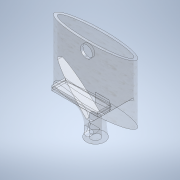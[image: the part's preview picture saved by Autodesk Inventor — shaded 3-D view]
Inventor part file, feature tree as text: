
AUTODESK INVENTOR PART (.ipt)
format: ipt  version: 2020 (Build 240168000, 168)  size: 277,504 bytes
history: native  units: mm
features: sketch x11, extrude x8, plane x3, chamfer x2, thicken_offset x2, loft x1, direct_edit x1, move_body x1
ambient origin geometry x8: Origin, YZ Plane, XZ Plane, XY Plane, X Axis, Y Axis, Z Axis, Center Point
bodies: Solid1 (feature_tree)
feature tree (29):
  sketch  "Sketch1"  dims[d0=20.0mm d1=20.0mm]
  plane  "Work Plane1"
  sketch  "Sketch2"  dims[d2=20.0mm d3=10.0mm]
  plane  "Work Plane2"
  loft  "Loft1"
  extrude  "Extrusion1"  Depth=10.0mm
  extrude  "Extrusion2"  Depth=10.0mm
  extrude  "Extrusion3"  TaperAngle=0.0deg  [1 undecoded]
  extrude  "Extrusion4"  Depth=10.0mm
  chamfer  "Chamfer1"  Distance=30.75mm
  chamfer  "Chamfer2"  Distance=30.0mm
  thicken_offset  "Thicken1"
  thicken_offset  "Thicken2"
  plane  "Work Plane3"
  extrude  "Extrusion5"  Depth=16.0mm TaperAngle=0.0deg
  extrude  "Extrusion6"  Depth=16.0mm TaperAngle=45.0deg
  extrude  "Extrusion7"  Depth=20.0mm
  direct_edit  "Direct Edit1"
  extrude  "Extrusion8"  Depth=20.0mm
  sketch  "Sketch3"  dims[d4=45.0mm d5=10.0mm]
  sketch  "Sketch4"  dims[d6=0.0mm d7=90.0deg d8=0.0mm d9=90.0deg]
  sketch  "Sketch5"  dims[d10=0.0mm d11=90.0deg d12=10.0mm d13=30.75mm d14=0.0mm d15=30.0mm d16=0.0mm]
  sketch  "Sketch6"  dims[d17=25.0mm d18=0.0mm d19=16.0mm d20=0.0mm]
  sketch  "Sketch7"  dims[d21=16.0mm d22=2.0mm d23=45.0deg d24=16.0mm d25=2.0mm d26=45.0deg]
  sketch  "Sketch8"  dims[d27=20.0mm d28=20.0mm]
  sketch  "Sketch9"  dims[d29=20.0mm d30=20.0mm]
  sketch  "Sketch10"  dims[d31=7.75mm]
  sketch  "Sketch11"  dims[d32=50.0mm d33=5.0mm d34=15.0mm d35=0.0mm d36=0.7mm d37=15.0mm d38=0.0mm d39=13.5mm d40=0.0mm d41=0.0mm d42=0.0mm d43=35.0mm d44=13.0mm d45=5.5mm d46=0.0mm]
  move_body  "Move1"
note: 1 required parameter value undecoded (feature->parameter linkage not recoverable at this tier; creation-order binding heuristic only, values carry confidence <= 0.55)
